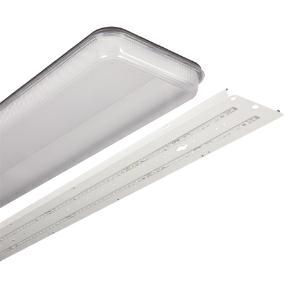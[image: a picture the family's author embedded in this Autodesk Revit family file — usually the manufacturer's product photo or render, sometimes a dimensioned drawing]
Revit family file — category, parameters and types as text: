
# Revit family: 3f_filippi_-_kit_led_retrofit_con_schermo_in_policarbonato_3f_filippi_-_a5013_-_kit_led_i3f75_a3f_90_a3f_d8abd7aca95db49d
name_source: partatom
category: Lighting Fixtures
units: mm (PartAtom-declared; Revit-internal decimal feet)

## family parameters
Cut with Voids When Loaded = No
Host = Face
Light Source = No
Part Type = Normal
Room Calculation Point = No
Round Connector Dimension = Use Diameter
Shared = No

## types (1)
- 3F Filippi - Kit LED Retrofit con schermo in policarbonato (1 x LED, 7351 lm, 49 W, 4000 K)
    Apparent Load = 49 VA
    Approval mark = ENEC
    CIE Flux Codes = 58 86 97 97 100
    Color Rendering = 80
    Color Temperature = 4000 K
    Control Gear = Electronic ballast
    Default Elevation = 1800 mm
    Description = Led retrofit kit suitable for Fluorescent Beta 2x i3F 75, A3F 90 and A3F 92 luminaires.

ILLUMINOTECHNICAL
Luminous efficiency 100% (DLOR 97%, ULOR 3%).
Initial luminous flux of the luminaire 7351 lm.
Symmetric concentrated distribution.
Installation Interdistance Transv.D = 0.89 x hu - Long.D = 1.19 x hu.
Tabular UGR (CIE 117 - 4H-8H; S=0.25H; 70/50/20): RUG 17.1 - 21.4.
Beam angle: 65° - 99°.
Luminous efficacy 150 lm/W.
Lifetime (L93/B10): 30000 h. (tq+25°C)
Lifetime (L90/B10): 50000 h. (tq+25°C)
Lifetime (L85/B10): 80000 h. (tq+25°C)
Lifetime (L80/B10): 100000 h. (tq+25°C)
Lifetime (L85/B10): 50000 h. (tq+35°C)
Sudden decreased luminous flux after 50000 hours: 0% (C0).
Photobiological safety in compliance with IEC/TR 62778: RG0 risk exempt, (IEC 62471).
In compliance with IEC/EN 62722-2-1 - IEC/EN 62717 standards.

SOURCE
2 linear LED modules 22W/840.
Energy efficiency class (UE 2019/2020 - UE 2019/2015): D.
CIE 13.3 Colour rendering index: CRI >80 (R9 <50%).
IES TM-30 Fidelity Index: Rf = 84 Rg = 95.
CCT nominal colour temperature 4000 K.
Colour initial tolerance (MacAdam): SDCM 3.

MECHANICAL
Diffuser in self-extinguishing V2 polycarbonate, photo-engraved interior, UV stabilised, injection moulded, with smooth outer surface, sealing gasket.
Concentrated flow recuperator, oversized, in specular aluminium with superficial titanium-magnesium treatment, non-iridescent.
Gear-tray unit in hot-galvanised steel, painted in white polyester, fixed to the housing by means of "Ribloc" rapid devices in galvanised steel, hinged opening.
Luminaire with limited surface temperature. - D - (EN 60598-2-24)
Dimensions: 1565x235 mm, height 135 mm. Weight 2.48 kg.
Glow-wire test resistance 850°C.

ELECTRICAL
Halogen Free electronic wiring 230V-50/60Hz, power factor 0.97, THD <25%, constant output current, SELV, class I, 1 driver.
Power of the luminaire 49 W.
CE - IEC 60598-1 - EN 60598-1.
SAFE FLICKER: PstLM=<1 and SVM=<0.4 (IEC TR 61547-1 and IEC TR 63158), to ensure a more comfortable and safe light.
Luminaire compliant with EN 60598-2-22 for power supply from a centralised emergency system CPSS (Central Power Supply System), not incorporated in the luminaire - high risk areas excluded. The default power and flux are 100% in AC and 100% in DC.
Ambient temperature from -20°C to +35°C.
Temperature class T6 max 85°C.
Relative humidity UR: <85%.

INSTALLATION
Retrofit.
Correct installation of the retrofit LED kit, compliant with EN 60598-1 and CE marked, inside the 3F Filippi - Beta 2x i3F 75, A3F 90 and A3F 92 Fluorescent luminaires must be only performed by qualified personnel to ensure compliance with the national installation standards.
Attention: to maintain the degree of protection of the device and for the purposes of validity of the guarantee of the new retrofit kits, it is imperative to replace the old cable guides (on the body of the device) with the new ones supplied.
All accessories dedicated to this product are available on the Catalog and on our website www.3F-Filippi.com.

WARNING
Fixture not suitable for cold stores with an ambient temperature <0°C and/or relative humidity >85%.
Luminaire designed for disposal/recycling at end-of-life.
Replaceable (LED only) light source by a professional. Replaceable control gear by a professional.
    Height = 135 mm
    Lamp = 1 x LED
    Lamp Light Flux = 7351 lm
    Lamp Power = 49 W
    Lamp count = 1
    Length = 1565 mm
    Lifetime = 50000 h
    Luminous efficacy = 150 lm/W
    Manufacturer = 3F Filippi
    ModVariant = No
    Model = 3F Filippi - A5013 - Kit LED I3F75,A3F 90,A3F 92-L1565-2X22W CONC+PC
    Mounting Place = Ceiling
    Mounting Type = Surface mounted
    Number of Poles = 1
    OnlyDefault = Yes
    Power Factor = 1
    Product Name = 3F Filippi - Kit LED Retrofit con schermo in policarbonato
    Product group = ceiling mounted luminaire
    ProductGroupID = 3
    Protection Class = Protection class I
    Protection Degree = Degree of protection
    RLX_Detail_Level = 1
    RLX_Emergency_Light_Flux = 0 lm
    RLX_Emergency_Type = 0
    RLX_Emergency_Type_DB = No
    RlxData = <blob elided: 72001 chars, md5=b3b6a566>
    Socket = socket
    Standby Power = 0 W
    System Light Flux = 7351 lm
    System Power = 49 W
    Type Comments = Product without accessories
    Type Image = 3ffilippi_a5013.jpg
    URL = http://relux.com
    VarID = ---
    Voltage = 0 V
    Weight = 0.00 kg
    Width = 235 mm

## geometry (parser evidence)
native form markers: Blend x4, Sweep x10
no freeform markers — native parametric forms only
